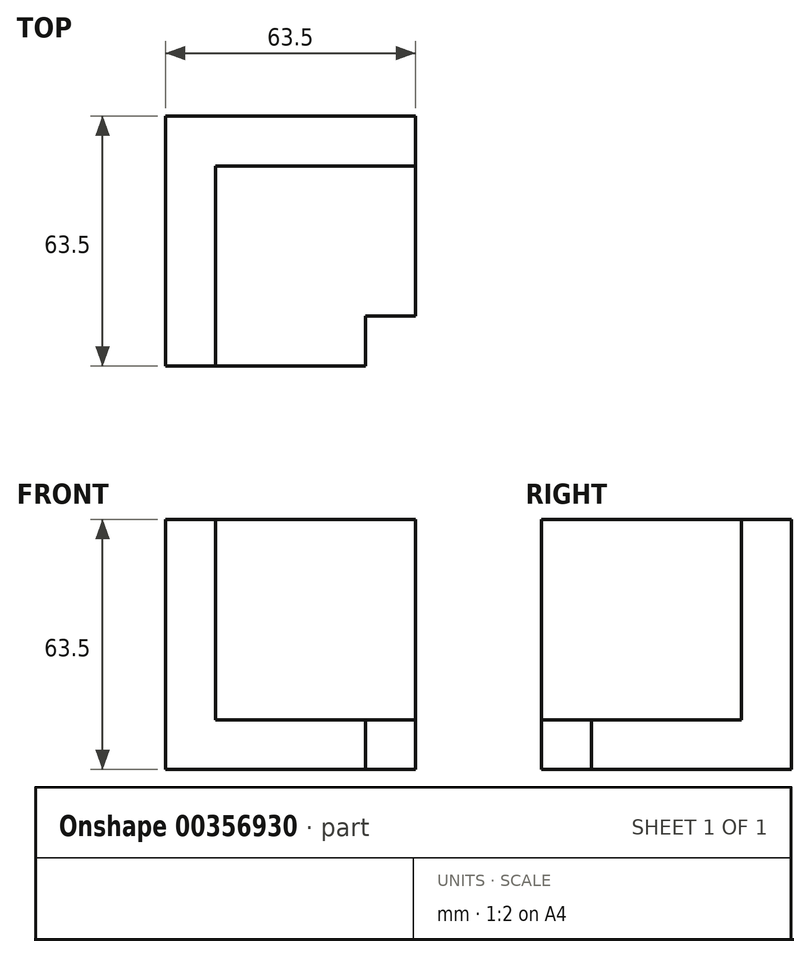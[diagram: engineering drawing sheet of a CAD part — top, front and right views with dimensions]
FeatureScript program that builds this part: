
annotation { "Feature Type Name" : "Feature", "Feature Type Description" : "" }
export const myFeature = defineFeature(function(context is Context, id is Id, definition is map)
    precondition{}
    {
        {
            var Q0;
            Q0=qCreatedBy(makeId("Front.planeOp"),FACE);
            var sketch = newSketch(context, id + "F0", { "sketchPlane" : qUnion([Q0])});
            skLineSegment(sketch, "E0.bottom", {"start": v(0, 0) * mm, "end": v(63.5, 0) * mm});
            skLineSegment(sketch, "E0.top", {"start": v(0, 63.5) * mm, "end": v(63.5, 63.5) * mm});
            skLineSegment(sketch, "E0.left", {"start": v(0, 0) * mm, "end": v(0, 63.5) * mm});
            skLineSegment(sketch, "E0.right", {"start": v(63.5, 0) * mm, "end": v(63.5, 63.5) * mm});
            skSolve(sketch);
        }
        {
            var Q0;
            Q0=makeQuery(id+"F0.imprint","IMPRINT",FACE,{"disambiguationData":[TD([[makeQuery(id+"F0.imprint","IMPRINT",EDGE,{"derivedFrom":sQuery(id+"F0.wireOp",EDGE,"E0.bottom")}),1.0]])]});
            extrude(context, id + "F1", {"entities" : qUnion([Q0]), "depth" : 63.5 * mm});
        }
        {
            var Q0;
            Q0=makeQuery(id+"F1.opExtrude","SWEPT_FACE",FACE,{"disambiguationData":[OSD([sQuery(id+"F0.wireOp",EDGE,"E0.top")])]});
            var sketch = newSketch(context, id + "F2", { "sketchPlane" : qUnion([Q0])});
            skLineSegment(sketch, "E1.bottom", {"start": v(63.5, -63.5) * mm, "end": v(12.7, -63.5) * mm});
            skLineSegment(sketch, "E1.top", {"start": v(63.5, -12.7) * mm, "end": v(12.7, -12.7) * mm});
            skLineSegment(sketch, "E1.left", {"start": v(63.5, -63.5) * mm, "end": v(63.5, -12.7) * mm});
            skLineSegment(sketch, "E1.right", {"start": v(12.7, -63.5) * mm, "end": v(12.7, -12.7) * mm});
            skSolve(sketch);
        }
        {
            var Q0;
            Q0=makeQuery(id+"F2.imprint","IMPRINT",FACE,{"disambiguationData":[TD([[makeQuery(id+"F2.imprint","IMPRINT",EDGE,{"derivedFrom":sQuery(id+"F2.wireOp",EDGE,"E1.bottom")}),1.0]])]});
            extrude(context, id + "F3", {"entities" : qUnion([Q0]), "operationType" : NewBodyOperationType.REMOVE, "oppositeDirection" : true, "depth" : 50.9 * mm});
        }
        {
            var Q0;
            Q0=makeQuery(id+"F3.boolean.opBoolean","COPY",FACE,{"derivedFrom":makeQuery(id+"F3.opExtrude","CAP_FACE",FACE,{"disambiguationData":[OSD([sQuery(id+"F2.wireOp",EDGE,"E1.bottom"),sQuery(id+"F2.wireOp",EDGE,"E1.top"),sQuery(id+"F2.wireOp",EDGE,"E1.left"),sQuery(id+"F2.wireOp",EDGE,"E1.right")])],"isStart":false})});
            var sketch = newSketch(context, id + "F4", { "sketchPlane" : qUnion([Q0])});
            skLineSegment(sketch, "E2.bottom", {"start": v(63.5, -63.5) * mm, "end": v(50.8, -63.5) * mm});
            skLineSegment(sketch, "E2.top", {"start": v(63.5, -50.8) * mm, "end": v(50.8, -50.8) * mm});
            skLineSegment(sketch, "E2.left", {"start": v(63.5, -63.5) * mm, "end": v(63.5, -50.8) * mm});
            skLineSegment(sketch, "E2.right", {"start": v(50.8, -63.5) * mm, "end": v(50.8, -50.8) * mm});
            skSolve(sketch);
        }
        {
            var Q0;
            Q0=makeQuery(id+"F4.imprint","IMPRINT",FACE,{"disambiguationData":[TD([[makeQuery(id+"F4.imprint","IMPRINT",EDGE,{"derivedFrom":sQuery(id+"F4.wireOp",EDGE,"E2.bottom")}),1.0]])]});
            extrude(context, id + "F5", {"entities" : qUnion([Q0]), "operationType" : NewBodyOperationType.REMOVE, "oppositeDirection" : true, "depth" : 25.4 * mm});
        }
    });
